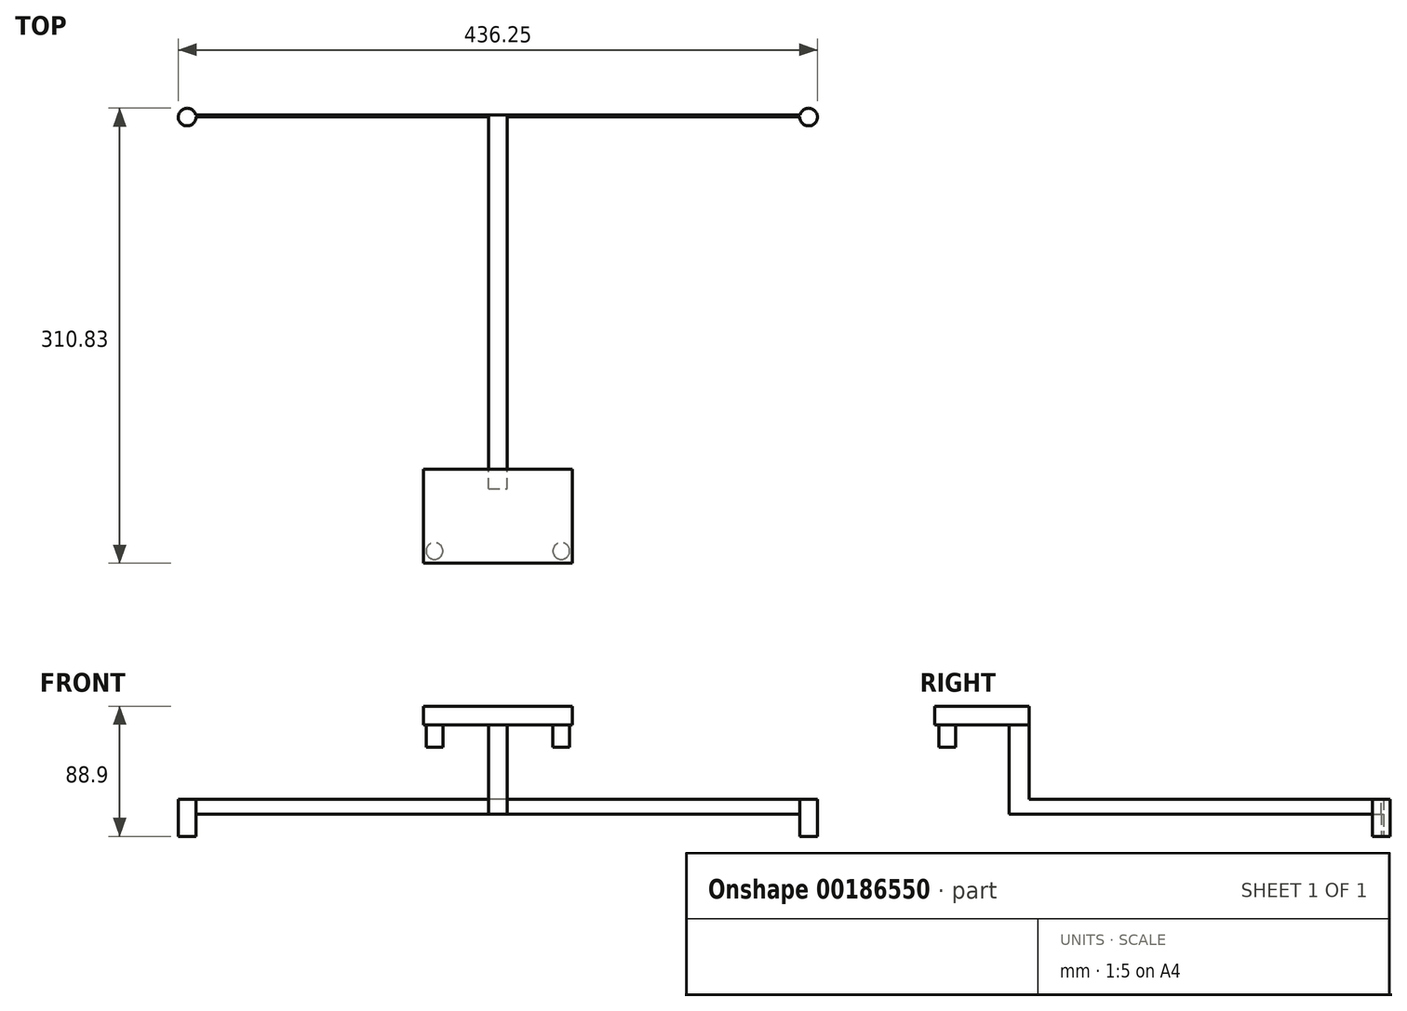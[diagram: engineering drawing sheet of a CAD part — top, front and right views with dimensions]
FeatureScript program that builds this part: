
annotation { "Feature Type Name" : "Feature", "Feature Type Description" : "" }
export const myFeature = defineFeature(function(context is Context, id is Id, definition is map)
    precondition{}
    {
        {
            var Q0;
            Q0=qCreatedBy(makeId("Top.planeOp"),FACE);
            var sketch = newSketch(context, id + "F0", { "sketchPlane" : qUnion([Q0])});
            skArc(sketch, "E0", {"start": v(-88.82, -5.17) * mm, "mid": v(-100.62, -7.54) * mm, "end": v(-88.61, -6.75) * mm});
            skLineSegment(sketch, "E1", {"start": v(-88.61, -6.75) * mm, "end": v(323.5, -6.75) * mm});
            skArc(sketch, "E2", {"start": v(323.5, -6.75) * mm, "mid": v(335.52, -7.54) * mm, "end": v(323.71, -5.17) * mm});
            skLineSegment(sketch, "E3", {"start": v(-86.5, -5.17) * mm, "end": v(323.71, -5.17) * mm});
            skLineSegment(sketch, "E4", {"start": v(-86.5, -5.17) * mm, "end": v(-88.82, -5.17) * mm});
            skSolve(sketch);
        }
        {
            var Q0;
            Q0=makeQuery(id+"F0.imprint","IMPRINT",FACE,{"disambiguationData":[TD([[makeQuery(id+"F0.imprint","IMPRINT",EDGE,{"derivedFrom":sQuery(id+"F0.wireOp",EDGE,"E0")}),1.0]])]});
            extrude(context, id + "F1", {"entities" : qUnion([Q0]), "depth" : 25.4 * mm});
        }
        {
            var Q0;
            Q0=makeQuery(id+"F1.opExtrude","CAP_FACE",FACE,{"disambiguationData":[OSD([sQuery(id+"F0.wireOp",EDGE,"E0"),sQuery(id+"F0.wireOp",EDGE,"E1"),sQuery(id+"F0.wireOp",EDGE,"E2"),sQuery(id+"F0.wireOp",EDGE,"E3"),sQuery(id+"F0.wireOp",EDGE,"E4")])],"isStart":true});
            var sketch = newSketch(context, id + "F2", { "sketchPlane" : qUnion([Q0])});
            skLineSegment(sketch, "E5", {"start": v(323.5, 6.75) * mm, "end": v(323.5, 5.17) * mm});
            skLineSegment(sketch, "E6", {"start": v(323.5, 5.17) * mm, "end": v(-88.82, 5.17) * mm});
            skLineSegment(sketch, "E7", {"start": v(-88.82, 5.17) * mm, "end": v(-88.61, 6.75) * mm});
            skLineSegment(sketch, "E8", {"start": v(-88.61, 6.75) * mm, "end": v(323.5, 6.75) * mm});
            skSolve(sketch);
        }
        {
            var Q0;
            Q0=makeQuery(id+"F2.imprint","IMPRINT",FACE,{"disambiguationData":[TD([[makeQuery(id+"F2.imprint","IMPRINT",EDGE,{"derivedFrom":sQuery(id+"F2.wireOp",EDGE,"E5")}),-1.0]])]});
            extrude(context, id + "F3", {"entities" : qUnion([Q0]), "operationType" : NewBodyOperationType.REMOVE, "oppositeDirection" : true, "depth" : 15.24 * mm});
        }
        {
            var Q0;
            Q0=makeQuery(id+"F1.opExtrude","SWEPT_FACE",FACE,{"disambiguationData":[OSD([sQuery(id+"F0.wireOp",EDGE,"E1")])]});
            var sketch = newSketch(context, id + "F4", { "sketchPlane" : qUnion([Q0])});
            skLineSegment(sketch, "E9", {"start": v(117.45, 25.4) * mm, "end": v(111.1, 25.4) * mm});
            skLineSegment(sketch, "E10", {"start": v(111.1, 25.4) * mm, "end": v(111.1, 15.24) * mm});
            skLineSegment(sketch, "E11", {"start": v(111.1, 15.24) * mm, "end": v(123.8, 15.24) * mm});
            skLineSegment(sketch, "E12", {"start": v(123.8, 15.24) * mm, "end": v(123.8, 25.4) * mm});
            skLineSegment(sketch, "E13", {"start": v(123.8, 25.4) * mm, "end": v(117.45, 25.4) * mm});
            skSolve(sketch);
        }
        {
            var Q0;
            Q0 = qSketchRegion(id + "F4", true);
            extrude(context, id + "F5", {"entities" : qUnion([Q0]), "operationType" : NewBodyOperationType.ADD, "depth" : 254 * mm});
        }
        {
            var Q0;
            Q0=makeQuery(id+"F5.boolean.opBoolean","MERGE",FACE,{"derivedFrom":[makeQuery(id+"F1.opExtrude","CAP_FACE",FACE,{"disambiguationData":[OSD([sQuery(id+"F0.wireOp",EDGE,"E0"),sQuery(id+"F0.wireOp",EDGE,"E1"),sQuery(id+"F0.wireOp",EDGE,"E2"),sQuery(id+"F0.wireOp",EDGE,"E3"),sQuery(id+"F0.wireOp",EDGE,"E4")])],"isStart":false}),makeQuery(id+"F5.opExtrude","SWEPT_FACE",FACE,{"disambiguationData":[OSD([sQuery(id+"F4.wireOp",EDGE,"E9"),sQuery(id+"F4.wireOp",EDGE,"E13")])]})]});
            var sketch = newSketch(context, id + "F6", { "sketchPlane" : qUnion([Q0])});
            skLineSegment(sketch, "E14", {"start": v(111.1, -260.75) * mm, "end": v(123.8, -260.75) * mm});
            skLineSegment(sketch, "E15", {"start": v(123.8, -260.75) * mm, "end": v(123.8, -247.23) * mm});
            skLineSegment(sketch, "E16", {"start": v(123.8, -247.23) * mm, "end": v(111.1, -247.23) * mm});
            skLineSegment(sketch, "E17", {"start": v(111.1, -247.23) * mm, "end": v(111.1, -260.75) * mm});
            skSolve(sketch);
        }
        {
            var Q0;
            Q0 = qSketchRegion(id + "F6", true);
            extrude(context, id + "F7", {"entities" : qUnion([Q0]), "operationType" : NewBodyOperationType.ADD, "depth" : 50.8 * mm});
        }
        {
            var Q0;
            Q0=makeQuery(id+"F7.opExtrude","CAP_FACE",FACE,{"disambiguationData":[OSD([sQuery(id+"F6.wireOp",EDGE,"E14"),sQuery(id+"F6.wireOp",EDGE,"E15"),sQuery(id+"F6.wireOp",EDGE,"E16"),sQuery(id+"F6.wireOp",EDGE,"E17")])],"isStart":false});
            var sketch = newSketch(context, id + "F8", { "sketchPlane" : qUnion([Q0])});
            skLineSegment(sketch, "E18", {"start": v(111.1, -247.23) * mm, "end": v(66.65, -247.23) * mm});
            skLineSegment(sketch, "E19", {"start": v(66.65, -247.23) * mm, "end": v(66.65, -260.75) * mm});
            skLineSegment(sketch, "E20", {"start": v(66.65, -260.75) * mm, "end": v(168.25, -260.75) * mm});
            skLineSegment(sketch, "E21", {"start": v(168.25, -260.75) * mm, "end": v(168.25, -247.23) * mm});
            skLineSegment(sketch, "E22", {"start": v(168.25, -247.23) * mm, "end": v(111.1, -247.23) * mm});
            skSolve(sketch);
        }
        {
            var Q0;
            Q0 = qSketchRegion(id + "F8", true);
            extrude(context, id + "F9", {"entities" : qUnion([Q0]), "operationType" : NewBodyOperationType.ADD, "depth" : 12.7 * mm});
        }
        {
            var Q0;
            Q0=makeQuery(id+"F9.boolean.opBoolean","MERGE",FACE,{"derivedFrom":[makeQuery(id+"F7.boolean.opBoolean","MERGE",FACE,{"derivedFrom":[makeQuery(id+"F5.opExtrude","CAP_FACE",FACE,{"disambiguationData":[OSD([sQuery(id+"F4.wireOp",EDGE,"E9"),sQuery(id+"F4.wireOp",EDGE,"E10"),sQuery(id+"F4.wireOp",EDGE,"E11"),sQuery(id+"F4.wireOp",EDGE,"E12"),sQuery(id+"F4.wireOp",EDGE,"E13")])],"isStart":false}),makeQuery(id+"F7.opExtrude","SWEPT_FACE",FACE,{"disambiguationData":[OSD([sQuery(id+"F6.wireOp",EDGE,"E14")])]})]}),makeQuery(id+"F9.opExtrude","SWEPT_FACE",FACE,{"disambiguationData":[OSD([sQuery(id+"F8.wireOp",EDGE,"E20")])]})]});
            var sketch = newSketch(context, id + "F10", { "sketchPlane" : qUnion([Q0])});
            skLineSegment(sketch, "E23", {"start": v(66.65, 76.2) * mm, "end": v(168.25, 76.2) * mm});
            skLineSegment(sketch, "E24", {"start": v(168.25, 76.2) * mm, "end": v(168.25, 88.9) * mm});
            skLineSegment(sketch, "E25", {"start": v(168.25, 88.9) * mm, "end": v(66.65, 88.9) * mm});
            skLineSegment(sketch, "E26", {"start": v(66.65, 88.9) * mm, "end": v(66.65, 76.2) * mm});
            skSolve(sketch);
        }
        {
            var Q0;
            {var subQ0=sQuery(id+"F10.wireOp",EDGE,"E24");Q0=makeQuery(id+"F10.imprint","IMPRINT",FACE,{"disambiguationData":[TD([[makeQuery(id+"F10.imprint","IMPRINT",EDGE,{"derivedFrom":subQ0}),-1.0]])]});}
            extrude(context, id + "F11", {"entities" : qUnion([Q0]), "operationType" : NewBodyOperationType.ADD, "depth" : 50.8 * mm});
        }
        {
            var Q0;
            {var subQ1=sQuery(id+"F8.wireOp",EDGE,"E21");var subQ2=sQuery(id+"F4.wireOp",EDGE,"E12");var subQ3=sQuery(id+"F4.wireOp",EDGE,"E10");var subQ6=sQuery(id+"F8.wireOp",EDGE,"E22");var subQ7=sQuery(id+"F8.wireOp",EDGE,"E18");var subQ9=sQuery(id+"F8.wireOp",EDGE,"E20");var subQ11=sQuery(id+"F8.wireOp",EDGE,"E19");var subQ12=makeQuery(id+"F9.opExtrude","CAP_FACE",FACE,{"disambiguationData":[OSD([subQ7,subQ11,subQ9,subQ1,subQ6])],"isStart":true});Q0=makeQuery(id+"F11.boolean.opBoolean","MERGE",FACE,{"derivedFrom":[makeQuery(id+"F9.boolean.opBoolean","SPLIT",FACE,{"disambiguationData":[TD([makeQuery(id+"F5.opExtrude","SWEPT_FACE",FACE,{"disambiguationData":[OSD([subQ3])]})])],"derivedFrom":subQ12}),makeQuery(id+"F9.boolean.opBoolean","SPLIT",FACE,{"disambiguationData":[TD([makeQuery(id+"F5.opExtrude","SWEPT_FACE",FACE,{"disambiguationData":[OSD([subQ2])]})])],"derivedFrom":subQ12}),makeQuery(id+"F11.opExtrude","SWEPT_FACE",FACE,{"disambiguationData":[OSD([sQuery(id+"F10.wireOp",EDGE,"E23")])]})]});}
            var sketch = newSketch(context, id + "F12", { "sketchPlane" : qUnion([Q0])});
            skCircle(sketch, "E27", {"center": v(74.15, 303.12) * mm, "radius": 5.72 * mm});
            skCircle(sketch, "E28", {"center": v(160.74, 303.12) * mm, "radius": 5.72 * mm});
            skSolve(sketch);
        }
        {
            var Q0;
            Q0=makeQuery(id+"F12.imprint","IMPRINT",FACE,{"disambiguationData":[TD([[makeQuery(id+"F12.imprint","IMPRINT",EDGE,{"derivedFrom":sQuery(id+"F12.wireOp",EDGE,"E27")}),1.0]])]});
            var Q1;
            Q1=makeQuery(id+"F12.imprint","IMPRINT",FACE,{"disambiguationData":[TD([[makeQuery(id+"F12.imprint","IMPRINT",EDGE,{"derivedFrom":sQuery(id+"F12.wireOp",EDGE,"E28")}),1.0]])]});
            extrude(context, id + "F13", {"entities" : qUnion([Q0, Q1]), "operationType" : NewBodyOperationType.ADD, "depth" : 15.24 * mm});
        }
    });
